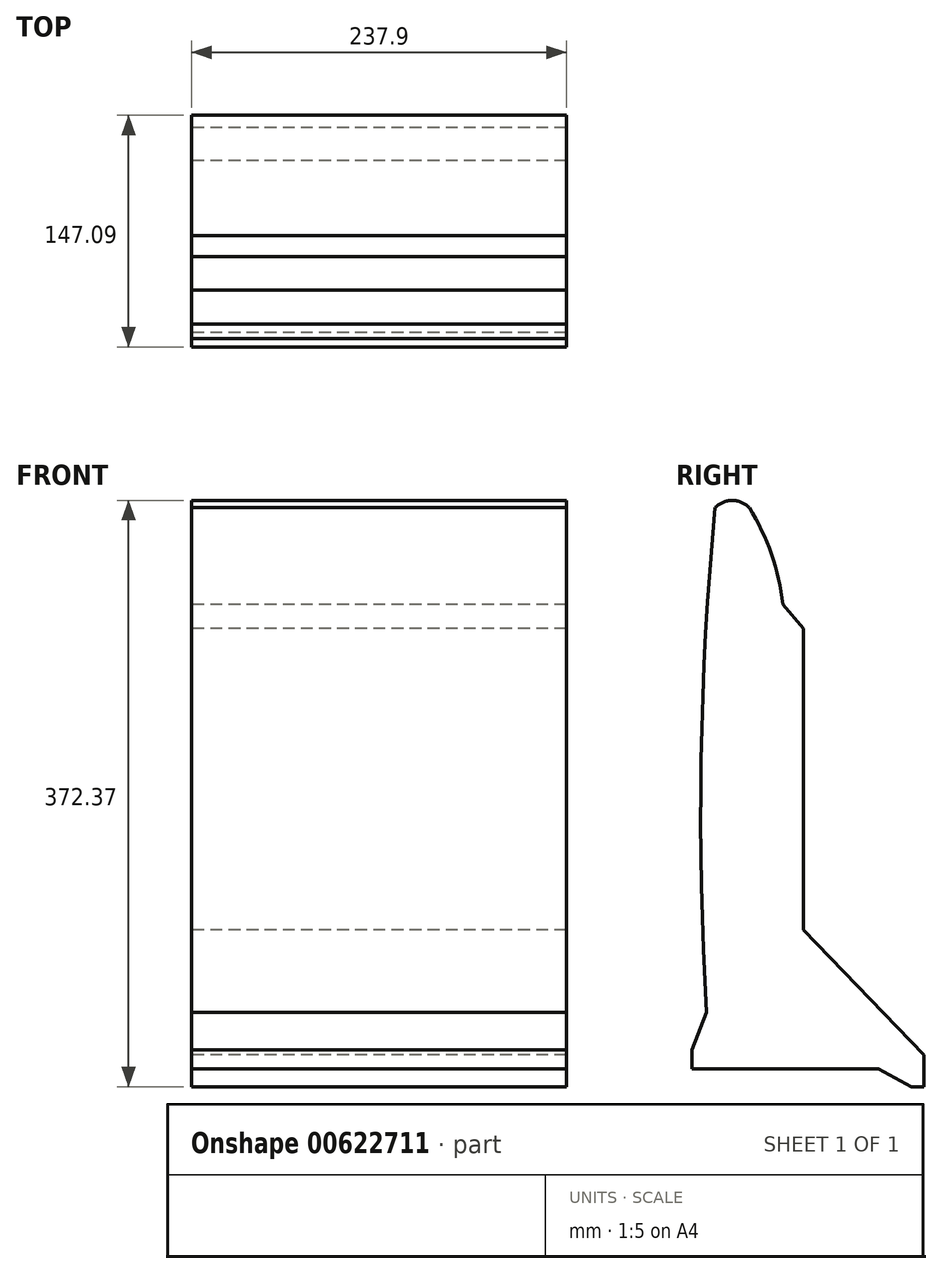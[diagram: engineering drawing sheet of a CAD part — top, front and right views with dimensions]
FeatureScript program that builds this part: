
annotation { "Feature Type Name" : "Feature", "Feature Type Description" : "" }
export const myFeature = defineFeature(function(context is Context, id is Id, definition is map)
    precondition{}
    {
        {
            var Q0;
            Q0=qCreatedBy(makeId("Top.planeOp"),FACE);
            var sketch = newSketch(context, id + "F0", { "sketchPlane" : qUnion([Q0])});
            skLineSegment(sketch, "E0.bottom", {"start": v(-108.59, 76.83) * mm, "end": v(129.31, 76.83) * mm});
            skLineSegment(sketch, "E0.top", {"start": v(-108.59, -95.67) * mm, "end": v(129.31, -95.67) * mm});
            skLineSegment(sketch, "E0.left", {"start": v(-108.59, 76.83) * mm, "end": v(-108.59, -95.67) * mm});
            skLineSegment(sketch, "E0.right", {"start": v(129.31, 76.83) * mm, "end": v(129.31, -95.67) * mm});
            skSolve(sketch);
        }
        {
            var Q0;
            Q0=makeQuery(id+"F0.imprint","IMPRINT",FACE,{"disambiguationData":[TD([[makeQuery(id+"F0.imprint","IMPRINT",EDGE,{"derivedFrom":sQuery(id+"F0.wireOp",EDGE,"E0.bottom")}),-1.0]])]});
            extrude(context, id + "F1", {"entities" : qUnion([Q0]), "depth" : 372.37 * mm, "offsetDistance" : 25 * mm});
        }
        {
            var Q0;
            Q0=makeQuery(id+"F1.opExtrude","SWEPT_FACE",FACE,{"disambiguationData":[OSD([sQuery(id+"F0.wireOp",EDGE,"E0.left")])]});
            var sketch = newSketch(context, id + "F2", { "sketchPlane" : qUnion([Q0])});
            skLineSegment(sketch, "E1", {"start": v(-76.83, 2.25) * mm, "end": v(-76.83, 20.25) * mm});
            skLineSegment(sketch, "E2", {"start": v(-76.83, 2.25) * mm, "end": v(-74.58, 0) * mm});
            skLineSegment(sketch, "E3", {"start": v(-74.58, 0) * mm, "end": v(-69.08, 0) * mm});
            skPoint(sketch, "E4", {"position": v(-8.33, 33.18) * mm});
            skLineSegment(sketch, "E5", {"start": v(-8.33, 33.18) * mm, "end": v(-0.33, 61.32) * mm});
            skLineSegment(sketch, "E6", {"start": v(-69.08, 0) * mm, "end": v(-8.33, 33.18) * mm});
            skLineSegment(sketch, "E7", {"start": v(-76.83, 20.25) * mm, "end": v(-0.33, 99.64) * mm});
            skLineSegment(sketch, "E8", {"start": v(-0.33, 99.64) * mm, "end": v(-0.33, 270.64) * mm});
            skLineSegment(sketch, "E9", {"start": v(-0.33, 270.64) * mm, "end": v(-0.33, 290.9) * mm});
            skLineSegment(sketch, "E10", {"start": v(-0.33, 99.64) * mm, "end": v(19.92, 99.64) * mm});
            skLineSegment(sketch, "E11", {"start": v(19.92, 99.64) * mm, "end": v(19.92, 270.64) * mm});
            skLineSegment(sketch, "E12", {"start": v(19.92, 270.64) * mm, "end": v(-0.33, 270.64) * mm});
            skLineSegment(sketch, "E13", {"start": v(-0.33, 61.32) * mm, "end": v(61.08, 47.25) * mm});
            skPoint(sketch, "E13.endSnap0", {"position": v(-4.33, 47.25) * mm});
            skLineSegment(sketch, "E14", {"start": v(-0.33, 290.9) * mm, "end": v(12.76, 306.35) * mm});
            skArc(sketch, "E15", {"start": v(34.04, 367.76) * mm, "mid": v(19.9, 338.27) * mm, "end": v(12.76, 306.35) * mm});
            skLineSegment(sketch, "E16", {"start": v(-26.1, 23.48) * mm, "end": v(95.67, 23.48) * mm});
            skLineSegment(sketch, "E17", {"start": v(95.67, 23.48) * mm, "end": v(95.67, 372.37) * mm});
            skLineSegment(sketch, "E18", {"start": v(-48.1, 11.45) * mm, "end": v(95.67, 11.45) * mm});
            skLineSegment(sketch, "E19", {"start": v(95.67, 11.45) * mm, "end": v(95.67, 23.48) * mm});
            skArc(sketch, "E20", {"start": v(55.67, 367.76) * mm, "mid": v(44.86, 372.37) * mm, "end": v(34.04, 367.76) * mm});
            skArc(sketch, "E21", {"start": v(61.08, 47.25) * mm, "mid": v(64.59, 207.61) * mm, "end": v(55.67, 367.76) * mm});
            skLineSegment(sketch, "E22", {"start": v(61.08, 47.25) * mm, "end": v(70.26, 23.48) * mm});
            skLineSegment(sketch, "E23", {"start": v(70.26, 23.48) * mm, "end": v(70.26, 11.45) * mm});
            skSolve(sketch);
        }
        {
            var Q0;
            {var subQ4=sQuery(id+"F2.wireOp",EDGE,"E18");Q0=makeQuery(id+"F2.imprint","IMPRINT",FACE,{"disambiguationData":[TD([[makeQuery(id+"F2.imprint","IMPRINT",EDGE,{"derivedFrom":subQ4}),-1.0]])]});}
            var Q1;
            {var subQ1=sQuery(id+"F2.wireOp",EDGE,"E7");Q1=makeQuery(id+"F2.imprint","IMPRINT",FACE,{"disambiguationData":[TD([[makeQuery(id+"F2.imprint","IMPRINT",EDGE,{"derivedFrom":subQ1}),1.0]])]});}
            var Q2;
            {var subQ4=sQuery(id+"F2.wireOp",EDGE,"E17");Q2=makeQuery(id+"F2.imprint","IMPRINT",FACE,{"disambiguationData":[TD([[makeQuery(id+"F2.imprint","IMPRINT",EDGE,{"derivedFrom":subQ4}),-1.0]])]});}
            var Q3;
            {var subQ0=sQuery(id+"F2.wireOp",EDGE,"E19");Q3=makeQuery(id+"F2.imprint","IMPRINT",FACE,{"disambiguationData":[TD([[makeQuery(id+"F2.imprint","IMPRINT",EDGE,{"derivedFrom":subQ0}),-1.0]])]});}
            extrude(context, id + "F3", {"entities" : qUnion([Q0, Q1, Q2, Q3]), "operationType" : NewBodyOperationType.REMOVE, "oppositeDirection" : true, "depth" : 10000 * mm, "offsetDistance" : 25 * mm});
        }
    });
